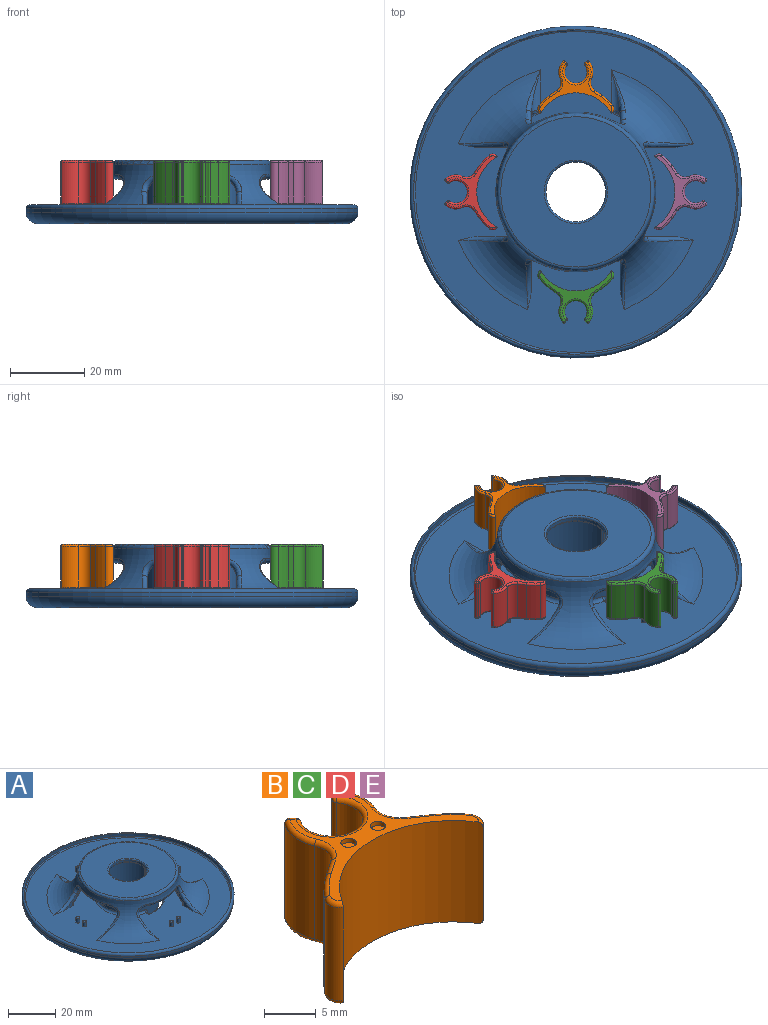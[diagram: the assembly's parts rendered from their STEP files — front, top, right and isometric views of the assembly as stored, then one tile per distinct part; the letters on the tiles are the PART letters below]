
ASSEMBLY  parts=5 mates=1
PART A: 175 faces, bbox 97.5x97.5x18.1 mm
  f0: cylinder r=0.75mm len=2.5mm, axis (0,0,-1), area 11.8mm2, adj f1,f25
  f1: plane 1.5x1.5mm, normal (0,0,1), area 1.8mm2, adj f0
  f2: cylinder r=0.75mm len=2.5mm, axis (0,0,-1), area 11.8mm2, adj f3,f25
  f3: plane 1.5x1.5mm, normal (0,0,1), area 1.8mm2, adj f2
  f4: cylinder r=0.75mm len=2.5mm, axis (0,0,-1), area 11.8mm2, adj f5,f25
  f5: plane 1.5x1.5mm, normal (0,0,1), area 1.8mm2, adj f4
  f6: cylinder r=0.75mm len=2.5mm, axis (0,0,-1), area 11.8mm2, adj f7,f25
  f7: plane 1.5x1.5mm, normal (0,0,1), area 1.8mm2, adj f6
  f8: cylinder r=0.75mm len=2.5mm, axis (0,0,-1), area 11.8mm2, adj f9,f25
  f9: plane 1.5x1.5mm, normal (0,0,1), area 1.8mm2, adj f8
  f10: cylinder r=0.75mm len=2.5mm, axis (0,0,-1), area 11.8mm2, adj f11,f25
  f11: plane 1.5x1.5mm, normal (0,0,1), area 1.8mm2, adj f10
  f12: torus R=23.48mm, axis (0,0,-1), area 13.2mm2, adj f13,f25,f142,f165
  f13: torus R=34.25mm, axis (0,0,1), area 340.9mm2, adj f12,f14,f15,f74,f75,f105,f106,f107
  f14: torus R=23.48mm, axis (0,0,-1), area 13.2mm2, adj f13,f25,f125,f148
  f15: torus R=23.48mm, axis (0,0,-1), area 15.3mm2, adj f13,f25,f104,f131
  f16: cylinder r=13.05mm len=26.1mm, axis (0,0,1), area 929.5mm2, adj f17,f20,f21,f36,f43,f47,f51,f58
  f17: plane 14.72x11.55mm, normal (0,0,1), area 29.1mm2, adj f16,f43,f46,f85,f87
  f18: cylinder r=11.05mm len=22.1mm, axis (0,0,1), area 835.1mm2, adj f35,f37,f42,f45,f46,f67,f78,f88
  f19: plane 83.5x83.5mm, normal (0,0,-1), area 4837.5mm2, adj f31,f47,f48,f49,f50,f51,f68,f83
  f20: plane 35.03x35.03mm, normal (0,0,-1), area 302.1mm2, adj f16,f69,f70,f71,f72,f73,f74
  f21: plane 14.72x11.55mm, normal (0,0,1), area 29.1mm2, adj f16,f35,f36,f77,f79
  f22: plane 29.1x25.1mm, normal (0,0,-1), area 291.7mm2, adj f36,f39,f40,f42,f43,f44,f95
  f23: cylinder r=44.75mm len=89.5mm, axis (0,0,1), area 281.2mm2, adj f28,f31
  f24: cylinder r=43.75mm len=87.5mm, axis (0,0,1), area 412.3mm2, adj f28,f30
  f25: plane 87.08x87.08mm, normal (0,0,1), area 4235.5mm2, adj f0,f2,f4,f6,f8,f10,f12,f14
  f26: torus R=34.25mm, axis (0,0,1), area 1425mm2, adj f25,f29,f113,f114,f115,f116,f117,f118
  f27: plane 40.5x40.5mm, normal (0,0,1), area 1058.6mm2, adj f29,f96
  f28: torus R=43.75mm, axis (0,0,1), area 438.1mm2, adj f23,f24
  f29: torus R=20.25mm, axis (0,0,-1), area 206.1mm2, adj f26,f27
  f30: torus R=43.25mm, axis (0,0,-1), area 215mm2, adj f24,f25
  f31: torus R=41.75mm, axis (0,0,1), area 1292.7mm2, adj f19,f23
  f32: cylinder r=15.05mm len=30.1mm, axis (0,0,1), area 100.8mm2, adj f49,f53,f58,f64
  f33: plane 13x1mm, normal (0.09,1,0), area 12.8mm2, adj f85,f87,f88,f90,f91,f92,f93
  f34: plane 13x1mm, normal (0.09,-1,0), area 12.8mm2, adj f77,f78,f79,f80,f82,f83,f84
  f35: torus R=11.55mm, axis (0,0,-1), area 13.9mm2, adj f18,f21,f37,f76
  f36: cylinder r=0.5mm len=3.04mm, axis (0.17,-0.98,0), area 3.5mm2, adj f16,f21,f22,f37,f38,f40,f69
  f37: bspline ~1.17x1.16mm, area 0.8mm2, adj f18,f35,f36,f40
  f38: sphere r=0.5mm, area 0.6mm2, adj f36,f39,f71
  f39: torus R=14.55mm, axis (0,0,-1), area 40mm2, adj f22,f38,f41,f73
  f40: torus R=1mm, axis (0,0,-1), area 0.8mm2, adj f22,f36,f37,f42
  f41: sphere r=0.5mm, area 0.6mm2, adj f39,f43,f72
  f42: torus R=10.55mm, axis (0,0,-1), area 23.1mm2, adj f18,f22,f40,f44
  f43: cylinder r=0.5mm len=3.04mm, axis (0.17,0.98,0), area 3.5mm2, adj f16,f17,f22,f41,f44,f45,f70
  f44: torus R=1mm, axis (0,0,-1), area 0.8mm2, adj f22,f42,f43,f45
  f45: bspline ~1.22x1.1mm, area 0.8mm2, adj f18,f43,f44,f46
  f46: torus R=11.55mm, axis (0,0,-1), area 13.9mm2, adj f17,f18,f45,f86
  f47: torus R=12.55mm, axis (0,0,1), area 16.2mm2, adj f16,f19,f57,f89
  f48: cylinder r=0.5mm len=3.04mm, axis (-0.17,-0.98,0), area 1.2mm2, adj f19,f55,f57
  f49: torus R=15.55mm, axis (0,0,1), area 41.3mm2, adj f19,f32,f55,f62
  f50: cylinder r=0.5mm len=3.04mm, axis (0.17,-0.98,0), area 1.2mm2, adj f19,f62,f65
  f51: torus R=12.55mm, axis (0,0,1), area 16.2mm2, adj f16,f19,f65,f81
  f52: cylinder r=0.5mm len=1.59mm, axis (-0.17,0.98,0), area 0.6mm2, adj f25,f61,f63
  f53: torus R=15.55mm, axis (0,0,1), area 41.3mm2, adj f25,f32,f56,f61
  f54: cylinder r=0.5mm len=1.59mm, axis (0.17,0.98,0), area 0.6mm2, adj f25,f56,f59
  f55: bspline ~1.64x1.42mm, area 0.6mm2, adj f48,f49,f58
  f56: bspline ~1.64x1.42mm, area 0.6mm2, adj f53,f54,f58
  f57: bspline ~1.54x1.33mm, area 0.5mm2, adj f47,f48,f58
  f58: cylinder r=1mm len=2mm, axis (0,0,1), area 6.3mm2, adj f16,f32,f55,f56,f57,f59
  f59: bspline ~1.83x1.61mm, area 2mm2, adj f16,f54,f58,f60
  f60: torus R=14.05mm, axis (0,0,1), area 57.3mm2, adj f16,f25,f59,f63
  f61: bspline ~1.64x1.42mm, area 0.6mm2, adj f52,f53,f64
  f62: bspline ~1.64x1.42mm, area 0.6mm2, adj f49,f50,f64
  f63: bspline ~1.83x1.69mm, area 2mm2, adj f16,f52,f60,f64
  f64: cylinder r=1mm len=2mm, axis (0,0,1), area 6.3mm2, adj f16,f32,f61,f62,f63,f65
  f65: bspline ~1.54x1.33mm, area 0.5mm2, adj f50,f51,f64
  f66: cone r=12.05mm half-angle=45deg, axis (0,0,-1), area 40.8mm2, adj f67,f68,f82,f92
  f67: torus R=12.05mm, axis (0,0,1), area 52.7mm2, adj f18,f66,f80,f90
  f68: torus R=12.46mm, axis (0,0,1), area 57.2mm2, adj f19,f66,f84,f93
  f69: cylinder r=0.5mm len=1.57mm, axis (0.17,-0.98,0), area 1.2mm2, adj f16,f20,f36,f71
  f70: cylinder r=0.5mm len=1.57mm, axis (-0.17,-0.98,0), area 1.2mm2, adj f16,f20,f43,f72
  f71: torus R=1mm, axis (0,0,-1), area 0.9mm2, adj f20,f38,f69,f73
  f72: torus R=1mm, axis (0,0,-1), area 0.9mm2, adj f20,f41,f70,f73
  f73: torus R=15.55mm, axis (0,0,-1), area 40.9mm2, adj f20,f39,f71,f72
  f74: torus R=17.52mm, axis (0,0,1), area 158.5mm2, adj f13,f20
  f75: torus R=23.48mm, axis (0,0,-1), area 15.3mm2, adj f13,f25,f112,f159
  f76: sphere r=0.5mm, area 0.5mm2, adj f35,f77,f78
  f77: cylinder r=0.5mm len=1.54mm, axis (-1,-0.09,0), area 1mm2, adj f21,f34,f76,f79
  f78: cylinder r=0.5mm len=12.09mm, axis (0,0,1), area 9.2mm2, adj f18,f34,f76,f80
  f79: cylinder r=0.5mm len=13.5mm, axis (0,0,1), area 10.7mm2, adj f16,f21,f34,f77,f81
  f80: bspline ~0.97x0.71mm, area 0.5mm2, adj f34,f67,f78,f82
  f81: sphere r=0.5mm, area 0.4mm2, adj f51,f79,f83
  f82: bspline ~2.46x2.42mm, area 0.5mm2, adj f34,f66,f80,f84
  f83: cylinder r=0.5mm len=0.51mm, axis (1,0.09,0), area 0.1mm2, adj f19,f34,f81,f84
  f84: bspline ~0.94x0.73mm, area 0.5mm2, adj f34,f68,f82,f83
  f85: cylinder r=0.5mm len=1.54mm, axis (1,-0.09,0), area 1mm2, adj f17,f33,f86,f87
  f86: sphere r=0.5mm, area 0.5mm2, adj f46,f85,f88
  f87: cylinder r=0.5mm len=13.5mm, axis (0,0,1), area 10.7mm2, adj f16,f17,f33,f85,f89
  f88: cylinder r=0.5mm len=12.09mm, axis (0,0,1), area 9.2mm2, adj f18,f33,f86,f90
  f89: sphere r=0.5mm, area 0.4mm2, adj f47,f87,f91
  f90: bspline ~0.97x0.71mm, area 0.5mm2, adj f33,f67,f88,f92
  f91: cylinder r=0.5mm len=0.51mm, axis (-1,0.09,0), area 0.1mm2, adj f19,f33,f89,f93
  f92: bspline ~2.46x2.42mm, area 0.5mm2, adj f33,f66,f90,f93
  f93: bspline ~0.94x0.73mm, area 0.5mm2, adj f33,f68,f91,f92
  f94: cylinder r=8.05mm len=16.1mm, axis (0,0,1), area 50.6mm2, adj f95,f96
  f95: torus R=8.55mm, axis (0,0,-1), area 40.6mm2, adj f22,f94
  f96: torus R=8.55mm, axis (0,0,-1), area 40.6mm2, adj f27,f94
  f97: plane 16x2.73mm, normal (0,0,-1), area 16.8mm2, adj f100,f101,f108,f116
  f98: plane 4.15x2.51mm, normal (-1,0,0), area 4mm2, adj f101,f103,f106,f114
  f99: plane 4.15x2.51mm, normal (1,0,0), area 4mm2, adj f100,f102,f110,f118
  f100: cylinder r=4mm len=4mm, axis (0,-1,0), area 8mm2, adj f97,f99,f109,f117
  f101: cylinder r=4mm len=4mm, axis (0,1,0), area 8mm2, adj f97,f98,f107,f115
  f102: cylinder r=2.5mm len=13.28mm, axis (0,1,0), area 22.4mm2, adj f25,f99,f111,f112,f119
  f103: cylinder r=2.5mm len=13.28mm, axis (0,-1,0), area 22.4mm2, adj f25,f98,f104,f105,f113
  f104: bspline ~3.09x1.93mm, area 1.8mm2, adj f15,f103,f105
  f105: bspline ~3.48x2.74mm, area 1.8mm2, adj f13,f103,f104,f106
  f106: bspline ~5.8x5.7mm, area 3.9mm2, adj f13,f98,f105,f107
  f107: bspline ~6.03x6.02mm, area 7.8mm2, adj f13,f101,f106,f108
  f108: torus R=19.55mm, axis (0,0,1), area 21.9mm2, adj f13,f97,f107,f109
  f109: bspline ~6.03x6.02mm, area 7.8mm2, adj f13,f100,f108,f110
  f110: bspline ~5.8x5.7mm, area 3.9mm2, adj f13,f99,f109,f111
  f111: bspline ~3.48x2.74mm, area 1.8mm2, adj f13,f102,f110,f112
  f112: bspline ~3.22x2.05mm, area 1.7mm2, adj f75,f102,f111
  f113: bspline ~12.03x3.96mm, area 7.4mm2, adj f26,f103,f114
  f114: bspline ~5.86x5.75mm, area 7mm2, adj f26,f98,f113,f115
  f115: bspline ~6.43x5.35mm, area 14.8mm2, adj f26,f101,f114,f116
  f116: torus R=20.58mm, axis (0,0,1), area 30.3mm2, adj f26,f97,f115,f117
  f117: bspline ~6.43x5.71mm, area 14.8mm2, adj f26,f100,f116,f118
  f118: bspline ~5.86x5.75mm, area 7mm2, adj f26,f99,f117,f119
  f119: bspline ~12.03x3.96mm, area 7.4mm2, adj f26,f102,f118
  f120: plane 16x2.73mm, normal (0,0,-1), area 16.8mm2, adj f123,f124,f128,f134
  f121: plane 8.79x5.01mm, normal (0,1,0), area 10.3mm2, adj f25,f124,f125,f126,f132
  f122: plane 8.79x5.01mm, normal (0,-1,0), area 10.3mm2, adj f25,f123,f130,f131,f136
  f123: cylinder r=4mm len=4mm, axis (-1,0,0), area 8mm2, adj f120,f122,f129,f135
  f124: cylinder r=4mm len=4mm, axis (1,0,0), area 8mm2, adj f120,f121,f127,f133
  f125: bspline ~2.88x2.06mm, area 2mm2, adj f14,f25,f121,f126
  f126: bspline ~6.88x6.58mm, area 5.7mm2, adj f13,f121,f125,f127
  f127: bspline ~6.03x6.02mm, area 7.8mm2, adj f13,f124,f126,f128
  f128: torus R=19.55mm, axis (0,0,1), area 21.9mm2, adj f13,f120,f127,f129
  f129: bspline ~6.03x6.02mm, area 7.8mm2, adj f13,f123,f128,f130
  f130: bspline ~6.88x6.58mm, area 5.7mm2, adj f13,f122,f129,f131
  f131: bspline ~2.88x2.06mm, area 2mm2, adj f15,f25,f122,f130
  f132: bspline ~15.47x8.16mm, area 20.9mm2, adj f25,f26,f121,f133
  f133: bspline ~6.43x5.35mm, area 14.8mm2, adj f26,f124,f132,f134
  f134: torus R=20.58mm, axis (0,0,1), area 30.3mm2, adj f26,f120,f133,f135
  f135: bspline ~6.43x5.71mm, area 14.8mm2, adj f26,f123,f134,f136
  f136: bspline ~15.47x8.16mm, area 20.9mm2, adj f25,f26,f122,f135
  f137: plane 16x2.73mm, normal (0,0,-1), area 16.8mm2, adj f140,f141,f145,f151
  f138: plane 8.79x5.01mm, normal (1,0,0), area 10.3mm2, adj f25,f141,f142,f143,f149
  f139: plane 8.79x5.01mm, normal (-1,0,0), area 10.3mm2, adj f25,f140,f147,f148,f153
  f140: cylinder r=4mm len=4mm, axis (0,1,0), area 8mm2, adj f137,f139,f146,f152
  f141: cylinder r=4mm len=4mm, axis (0,-1,0), area 8mm2, adj f137,f138,f144,f150
  f142: bspline ~2.88x2.06mm, area 2mm2, adj f12,f25,f138,f143
  f143: bspline ~6.88x6.58mm, area 5.7mm2, adj f13,f138,f142,f144
  f144: bspline ~6.03x6.02mm, area 7.8mm2, adj f13,f141,f143,f145
  f145: torus R=19.55mm, axis (0,0,1), area 21.9mm2, adj f13,f137,f144,f146
  f146: bspline ~6.03x6.02mm, area 7.8mm2, adj f13,f140,f145,f147
  f147: bspline ~6.88x6.58mm, area 5.7mm2, adj f13,f139,f146,f148
  f148: bspline ~2.88x2.06mm, area 2mm2, adj f14,f25,f139,f147
  f149: bspline ~15.47x8.16mm, area 20.9mm2, adj f25,f26,f138,f150
  f150: bspline ~5.72x5.71mm, area 14.8mm2, adj f26,f141,f149,f151
  f151: torus R=20.58mm, axis (0,0,1), area 30.3mm2, adj f26,f137,f150,f152
  f152: bspline ~6.43x5.71mm, area 14.8mm2, adj f26,f140,f151,f153
  f153: bspline ~15.47x8.16mm, area 20.9mm2, adj f25,f26,f139,f152
  f154: plane 16x2.73mm, normal (0,0,-1), area 16.8mm2, adj f157,f158,f162,f168
  f155: plane 8.79x5.01mm, normal (0,-1,0), area 10.3mm2, adj f25,f158,f159,f160,f166
  f156: plane 8.79x5.01mm, normal (0,1,0), area 10.3mm2, adj f25,f157,f164,f165,f170
  f157: cylinder r=4mm len=4mm, axis (1,0,0), area 8mm2, adj f154,f156,f163,f169
  f158: cylinder r=4mm len=4mm, axis (-1,0,0), area 8mm2, adj f154,f155,f161,f167
  f159: bspline ~2.88x2.06mm, area 2mm2, adj f25,f75,f155,f160
  f160: bspline ~6.88x6.58mm, area 5.7mm2, adj f13,f155,f159,f161
  f161: bspline ~6.03x6.02mm, area 7.8mm2, adj f13,f158,f160,f162
  f162: torus R=19.55mm, axis (0,0,1), area 21.9mm2, adj f13,f154,f161,f163
  f163: bspline ~6.03x6.02mm, area 7.8mm2, adj f13,f157,f162,f164
  f164: bspline ~6.88x6.58mm, area 5.7mm2, adj f13,f156,f163,f165
  f165: bspline ~2.88x2.06mm, area 2mm2, adj f12,f25,f156,f164
  f166: bspline ~15.47x8.16mm, area 20.9mm2, adj f25,f26,f155,f167
  f167: bspline ~6.43x5.35mm, area 14.8mm2, adj f26,f158,f166,f168
  f168: torus R=20.58mm, axis (0,0,1), area 30.3mm2, adj f26,f154,f167,f169
  f169: bspline ~6.43x5.71mm, area 14.8mm2, adj f26,f157,f168,f170
  f170: bspline ~15.47x8.16mm, area 20.9mm2, adj f25,f26,f156,f169
  f171: cylinder r=0.75mm len=2.5mm, axis (0,0,-1), area 11.8mm2, adj f25,f172
  f172: plane 1.5x1.5mm, normal (0,0,1), area 1.8mm2, adj f171
  f173: cylinder r=0.75mm len=2.5mm, axis (0,0,-1), area 11.8mm2, adj f25,f174
  f174: plane 1.5x1.5mm, normal (0,0,1), area 1.8mm2, adj f173
PART B: 58 faces, bbox 20.7x14.3x12 mm
  f0: plane 19.47x13.22mm, normal (0,0,1), area 40.4mm2, adj f4,f20,f21,f22,f23,f24,f26,f28
  f1: cylinder r=4.6mm len=11mm, axis (0,0,-1), area 54.5mm2, adj f12,f19,f32,f49
  f2: plane 11x2.02mm, normal (-0.57,0.82,0), area 26.9mm2, adj f3,f12,f34,f51
  f3: cylinder r=12.55mm len=11mm, axis (0,0,-1), area 42.8mm2, adj f2,f14,f35,f52
  f4: cylinder r=11.05mm len=19.14mm, axis (0,0,-1), area 277.5mm2, adj f0,f11,f14,f15,f20,f36,f37,f53
  f5: cylinder r=12.55mm len=11mm, axis (0,0,-1), area 42.8mm2, adj f6,f15,f21,f38
  f6: plane 11x2.02mm, normal (0.57,0.82,0), area 26.9mm2, adj f5,f13,f22,f39
  f7: cylinder r=4.6mm len=11mm, axis (0,0,-1), area 54.5mm2, adj f13,f16,f24,f41
  f8: plane 11x0.43mm, normal (-0.71,0.71,0), area 6.7mm2, adj f16,f17,f26,f43
  f9: cylinder r=3mm len=11mm, axis (0,0,-1), area 146mm2, adj f17,f18,f28,f45
  f10: plane 11x0.43mm, normal (0.71,0.71,0), area 6.7mm2, adj f18,f19,f30,f47
  f11: plane 19.47x13.22mm, normal (0,0,-1), area 43.9mm2, adj f4,f37,f38,f39,f40,f41,f43,f45
  f12: cylinder r=2.5mm len=11mm, axis (0,0,-1), area 38mm2, adj f1,f2,f33,f50
  f13: cylinder r=2.5mm len=11mm, axis (0,0,-1), area 38mm2, adj f6,f7,f23,f40
  f14: cylinder r=1.5mm len=11mm, axis (0,0,1), area 27mm2, adj f3,f4,f36,f53
  f15: cylinder r=1.5mm len=11mm, axis (0,0,1), area 27mm2, adj f4,f5,f20,f37
  f16: cylinder r=0.5mm len=11mm, axis (0,0,-1), area 9.3mm2, adj f7,f8,f25,f42
  f17: cylinder r=0.5mm len=11mm, axis (0,0,-1), area 7.9mm2, adj f8,f9,f27,f44
  f18: cylinder r=0.5mm len=11mm, axis (0,0,-1), area 7.9mm2, adj f9,f10,f29,f46
  f19: cylinder r=0.5mm len=11mm, axis (0,0,-1), area 9.3mm2, adj f1,f10,f31,f48
  f20: torus R=1mm, axis (0,0,1), area 1.7mm2, adj f0,f4,f15,f21
  f21: torus R=12.05mm, axis (0,0,1), area 3mm2, adj f0,f5,f20,f22
  f22: cylinder r=0.5mm len=2.3mm, axis (0.82,-0.57,0), area 1.9mm2, adj f0,f6,f21,f23
  f23: torus R=3mm, axis (0,0,1), area 2.9mm2, adj f0,f13,f22,f24
  f24: torus R=4.1mm, axis (0,0,1), area 3.7mm2, adj f0,f7,f23,f25
  f25: sphere r=0.5mm, area 0.4mm2, adj f16,f24,f26
  f26: cylinder r=0.5mm len=0.78mm, axis (0.71,0.71,0), area 0.5mm2, adj f0,f8,f25,f27
  f27: sphere r=0.5mm, area 0.4mm2, adj f17,f26,f28
  f28: torus R=3.5mm, axis (0,0,1), area 11.1mm2, adj f0,f9,f27,f29
  f29: sphere r=0.5mm, area 0.4mm2, adj f18,f28,f30
  f30: cylinder r=0.5mm len=0.78mm, axis (0.71,-0.71,0), area 0.5mm2, adj f0,f10,f29,f31
  f31: sphere r=0.5mm, area 0.4mm2, adj f19,f30,f32
  f32: torus R=4.1mm, axis (0,0,1), area 3.7mm2, adj f0,f1,f31,f33
  f33: torus R=3mm, axis (0,0,1), area 2.9mm2, adj f0,f12,f32,f34
  f34: cylinder r=0.5mm len=2.3mm, axis (0.82,0.57,0), area 1.9mm2, adj f0,f2,f33,f35
  f35: torus R=12.05mm, axis (0,0,1), area 3mm2, adj f0,f3,f34,f36
  f36: torus R=1mm, axis (0,0,1), area 1.7mm2, adj f0,f4,f14,f35
  f37: torus R=1mm, axis (0,0,1), area 1.7mm2, adj f4,f11,f15,f38
  f38: torus R=12.05mm, axis (0,0,1), area 3mm2, adj f5,f11,f37,f39
  f39: cylinder r=0.5mm len=2.3mm, axis (-0.82,0.57,0), area 1.9mm2, adj f6,f11,f38,f40
  f40: torus R=3mm, axis (0,0,1), area 2.9mm2, adj f11,f13,f39,f41
  f41: torus R=4.1mm, axis (0,0,1), area 3.7mm2, adj f7,f11,f40,f42
  f42: sphere r=0.5mm, area 0.4mm2, adj f16,f41,f43
  f43: cylinder r=0.5mm len=0.78mm, axis (-0.71,-0.71,0), area 0.5mm2, adj f8,f11,f42,f44
  f44: sphere r=0.5mm, area 0.4mm2, adj f17,f43,f45
  f45: torus R=3.5mm, axis (0,0,1), area 11.1mm2, adj f9,f11,f44,f46
  f46: sphere r=0.5mm, area 0.4mm2, adj f18,f45,f47
  f47: cylinder r=0.5mm len=0.78mm, axis (-0.71,0.71,0), area 0.5mm2, adj f10,f11,f46,f48
  f48: sphere r=0.5mm, area 0.4mm2, adj f19,f47,f49
  f49: torus R=4.1mm, axis (0,0,1), area 3.7mm2, adj f1,f11,f48,f50
  f50: torus R=3mm, axis (0,0,1), area 2.9mm2, adj f11,f12,f49,f51
  f51: cylinder r=0.5mm len=2.3mm, axis (-0.82,-0.57,0), area 1.9mm2, adj f2,f11,f50,f52
  f52: torus R=12.05mm, axis (0,0,1), area 3mm2, adj f3,f11,f51,f53
  f53: torus R=1mm, axis (0,0,1), area 1.7mm2, adj f4,f11,f14,f52
  f54: cylinder r=0.75mm len=1.5mm, axis (0,0,1), area 2.4mm2, adj f0,f55
  f55: plane 1.5x1.5mm, normal (0,0,1), area 1.8mm2, adj f54
  f56: cylinder r=0.75mm len=1.5mm, axis (0,0,1), area 2.4mm2, adj f0,f57
  f57: plane 1.5x1.5mm, normal (0,0,1), area 1.8mm2, adj f56
PART C: same geometry as B
PART D: same geometry as B
PART E: same geometry as B
PLACE A t=(0,0,-17)mm
PLACE B rot(axis=(0,1,0),180deg) t=(0,15.65,0)mm
PLACE C rot(axis=(1,0,0),180deg) t=(0,-15.65,0)mm
PLACE D rot(axis=(0.71,-0.71,0),180deg) t=(-15.65,0,0)mm
PLACE E rot(axis=(0.71,0.71,0),180deg) t=(15.65,0,0)mm
MATE fastened B.f54 <-> A.f171  axis (0,0,-1) through (-2,28,-11.5)mm
